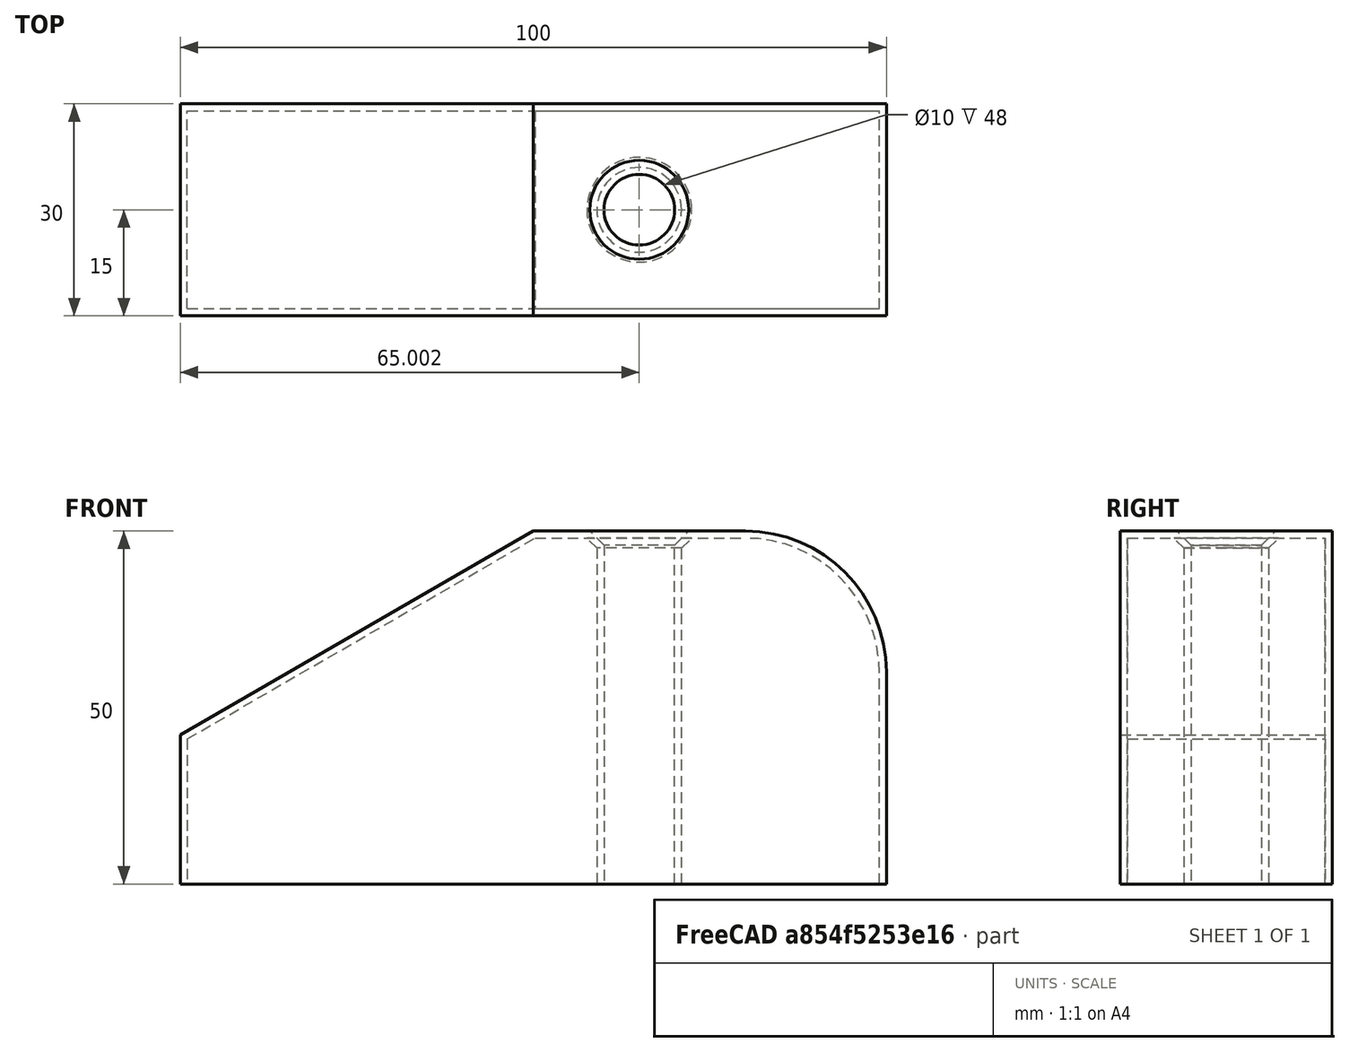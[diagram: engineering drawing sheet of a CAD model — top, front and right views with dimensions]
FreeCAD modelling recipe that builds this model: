
FCSTD DOCUMENT  (FreeCAD 0.20R29410 (Git))
Label: Creating a simple part with Part WB_Hollowed
License: All rights reserved
LicenseURL: http://en.wikipedia.org/wiki/All_rights_reserved
objects: Part::Cut×3, Part::Box×2, Part::Fillet×1, Part::Cylinder×1, Part::Cone×1, Part::Thickness×1
note: 9 computed .brp shape members not serialized (recipe doc carries the construction recipe); baked Part::Feature solids carry a one-line shape summary decoded from their .brp

FEATURE [Part::Box] Box  label="Cube"
  AttacherType = Attacher::AttachEngine3D
  Height = 50
  Length = 100
  Width = 30
FEATURE [Part::Fillet] Fillet
  Base = -> Box
  Edges = 1 edges r=20: [Edge6]
FEATURE [Part::Box] Box001  label="Cube001"
  AttacherType = Attacher::AttachEngine3D
  Height = 30
  Length = 60
  Placement = pos=(0,0,21.13) rot=(0,1,0;-0.523599rad)
  Width = 30
FEATURE [Part::Cut] Cut
  Base = -> Fillet
  Tool = -> Box001
FEATURE [Part::Cylinder] Cylinder
  Angle = 360
  AttacherType = Attacher::AttachEngine3D
  FirstAngle = 0
  Height = 50
  Placement = pos=(65.0022,15,0) rot=(0,0,1;0rad)
  Radius = 5
  SecondAngle = 0
FEATURE [Part::Cut] Cut001
  Base = -> Cut
  Tool = -> Cylinder
FEATURE [Part::Cone] Cone
  Angle = 360
  AttacherType = Attacher::AttachEngine3D
  Height = 7
  Placement = pos=(65.0022,15,43) rot=(0,0,1;0rad)
  Radius1 = 0
  Radius2 = 7
FEATURE [Part::Cut] Cut002
  Base = -> Cut001
  Tool = -> Cone
FEATURE [Part::Thickness] Thickness
  Faces = -> Cut002 [Face3]
  Intersection = false
  Join = 0
  Mode = 0
  SelfIntersection = false
  Value = -1
